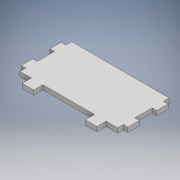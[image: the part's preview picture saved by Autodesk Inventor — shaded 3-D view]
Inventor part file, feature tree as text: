
AUTODESK INVENTOR PART (.ipt)
format: ipt  version: 2018 (Build 220112000, 112)  size: 146,432 bytes
history: native  units: mm
features: extrude x3, sketch x3, plane x1, mirror x1, projected_geometry x1
ambient origin geometry x8: Origin, YZ Plane, XZ Plane, XY Plane, X Axis, Y Axis, Z Axis, Center Point
bodies: Solid1 (feature_tree)
feature tree (9):
  extrude  "Extrusion1"  Depth=45.0mm
  extrude  "Extrusion2"  Depth=4.0mm
  plane  "Work Plane1"
  mirror  "Mirror1"
  extrude  "Extrusion3"  Depth=4.0mm
  sketch  "Sketch1"  dims[d0=85.0mm d1=45.0mm]
  sketch  "Sketch2"  dims[d2=4.0mm d3=0.0mm d4=4.0mm]
  projected_geometry  "Projected Loop1"
  sketch  "Sketch3"  dims[d5=10.0mm d6=4.0mm d7=10.0mm d8=5.0mm d9=5.0mm d10=4.0mm d11=0.0mm d12=10.0mm d13=8.0mm d14=10.0mm d15=8.0mm d18=4.0mm d19=0.0mm]
